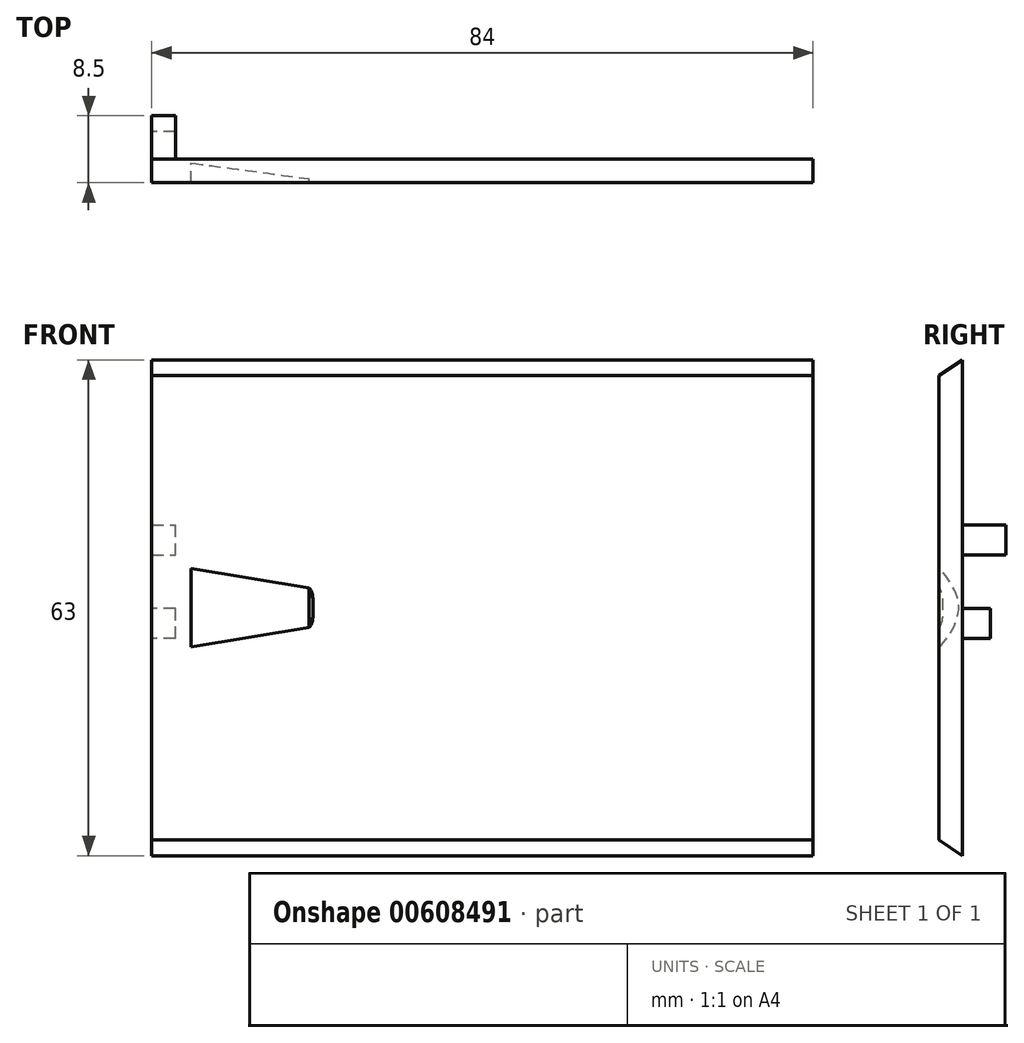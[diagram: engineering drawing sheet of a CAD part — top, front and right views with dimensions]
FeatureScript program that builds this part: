
annotation { "Feature Type Name" : "Feature", "Feature Type Description" : "" }
export const myFeature = defineFeature(function(context is Context, id is Id, definition is map)
    precondition{}
    {
        {
            var Q0;
            Q0=qCreatedBy(makeId("Front.planeOp"),FACE);
            var sketch = newSketch(context, id + "F0", { "sketchPlane" : qUnion([Q0])});
            skLineSegment(sketch, "E0.bottom", {"start": v(0, 0) * mm, "end": v(87, 0) * mm});
            skLineSegment(sketch, "E0.left", {"start": v(0, 0) * mm, "end": v(0, 81) * mm});
            skLineSegment(sketch, "E0.right", {"start": v(87, 0) * mm, "end": v(87, 81) * mm});
            skLineSegment(sketch, "E1", {"start": v(3, 3) * mm, "end": v(3, 35.5) * mm});
            skLineSegment(sketch, "E2", {"start": v(3, 35.5) * mm, "end": v(23.2, 35.5) * mm});
            skLineSegment(sketch, "E3", {"start": v(23.2, 35.5) * mm, "end": v(23.2, 37.5) * mm});
            skLineSegment(sketch, "E4", {"start": v(23.2, 37.5) * mm, "end": v(3, 37.5) * mm});
            skLineSegment(sketch, "E5", {"start": v(3, 37.5) * mm, "end": v(3, 43.2) * mm});
            skLineSegment(sketch, "E6", {"start": v(16.4, 45.2) * mm, "end": v(16.4, 42.3) * mm});
            skLineSegment(sketch, "E7", {"start": v(27.8, 41.8) * mm, "end": v(37.8, 41.8) * mm});
            skLineSegment(sketch, "E8", {"start": v(28.7, 37.5) * mm, "end": v(27.9, 37.5) * mm});
            skLineSegment(sketch, "E9", {"start": v(27.9, 37.5) * mm, "end": v(27.9, 35.5) * mm});
            skLineSegment(sketch, "E10", {"start": v(84, 62) * mm, "end": v(84, 3) * mm});
            skLineSegment(sketch, "E11", {"start": v(84, 3) * mm, "end": v(3, 3) * mm});
            skLineSegment(sketch, "E12", {"start": v(3.2, 37.6) * mm, "end": v(3.2, 39.1) * mm, "construction": true});
            skLineSegment(sketch, "E13", {"start": v(3.2, 39.1) * mm, "end": v(2.2, 39.1) * mm, "construction": true});
            skLineSegment(sketch, "E14", {"start": v(2.2, 39.1) * mm, "end": v(2.2, 43) * mm, "construction": true});
            skLineSegment(sketch, "E15", {"start": v(2.2, 43) * mm, "end": v(11.2, 43) * mm, "construction": true});
            skLineSegment(sketch, "E16", {"start": v(11.2, 43) * mm, "end": v(11.2, 42.1) * mm, "construction": true});
            skLineSegment(sketch, "E17", {"start": v(11.2, 42.1) * mm, "end": v(23.7, 42.1) * mm, "construction": true});
            skLineSegment(sketch, "E18", {"start": v(23.7, 42.1) * mm, "end": v(23.7, 42.6) * mm, "construction": true});
            skLineSegment(sketch, "E19", {"start": v(23.7, 42.6) * mm, "end": v(27.7, 42.6) * mm, "construction": true});
            skLineSegment(sketch, "E20", {"start": v(27.7, 35.6) * mm, "end": v(23.7, 35.6) * mm, "construction": true});
            skLineSegment(sketch, "E21", {"start": v(23.7, 35.6) * mm, "end": v(23.7, 37.6) * mm, "construction": true});
            skLineSegment(sketch, "E22", {"start": v(23.7, 37.6) * mm, "end": v(3.2, 37.6) * mm, "construction": true});
            skLineSegment(sketch, "E23", {"start": v(27.7, 35.6) * mm, "end": v(27.7, 37.6) * mm, "construction": true});
            skLineSegment(sketch, "E24", {"start": v(27.7, 37.6) * mm, "end": v(28.2, 37.6) * mm, "construction": true});
            skLineSegment(sketch, "E25", {"start": v(3, 43.2) * mm, "end": v(11.4, 43.2) * mm});
            skLineSegment(sketch, "E26", {"start": v(11.4, 43.2) * mm, "end": v(11.4, 42.3) * mm});
            skLineSegment(sketch, "E27", {"start": v(11.4, 42.3) * mm, "end": v(16.4, 42.3) * mm});
            skLineSegment(sketch, "E28", {"start": v(28.2, 37.6) * mm, "end": v(28.2, 39.6) * mm, "construction": true});
            skLineSegment(sketch, "E29", {"start": v(28.2, 39.6) * mm, "end": v(27.7, 39.6) * mm, "construction": true});
            skLineSegment(sketch, "E30", {"start": v(27.7, 39.6) * mm, "end": v(27.7, 42.6) * mm, "construction": true});
            skLineSegment(sketch, "E31.bottom", {"start": v(5, 3.5) * mm, "end": v(82, 3.5) * mm, "construction": true});
            skLineSegment(sketch, "E31.top", {"start": v(5, 25.5) * mm, "end": v(82, 25.5) * mm, "construction": true});
            skLineSegment(sketch, "E31.left", {"start": v(5, 3.5) * mm, "end": v(5, 25.5) * mm, "construction": true});
            skLineSegment(sketch, "E31.right", {"start": v(82, 3.5) * mm, "end": v(82, 25.5) * mm, "construction": true});
            skLineSegment(sketch, "E32", {"start": v(28.7, 37.5) * mm, "end": v(28.7, 39.8) * mm});
            skLineSegment(sketch, "E33", {"start": v(28.7, 39.8) * mm, "end": v(27.8, 39.8) * mm});
            skLineSegment(sketch, "E34", {"start": v(27.8, 39.8) * mm, "end": v(27.8, 41.8) * mm});
            skLineSegment(sketch, "E35", {"start": v(21.6, 54) * mm, "end": v(23.1, 54) * mm, "construction": true});
            skLineSegment(sketch, "E36", {"start": v(23.1, 54) * mm, "end": v(23.1, 52) * mm, "construction": true});
            skLineSegment(sketch, "E37", {"start": v(23.1, 52) * mm, "end": v(27.6, 52) * mm, "construction": true});
            skLineSegment(sketch, "E38", {"start": v(27.6, 52) * mm, "end": v(27.6, 54) * mm, "construction": true});
            skLineSegment(sketch, "E39", {"start": v(27.6, 54) * mm, "end": v(53.1, 54) * mm, "construction": true});
            skLineSegment(sketch, "E40", {"start": v(53.1, 54) * mm, "end": v(53.1, 52) * mm, "construction": true});
            skLineSegment(sketch, "E41", {"start": v(53.1, 52) * mm, "end": v(57.6, 52) * mm, "construction": true});
            skLineSegment(sketch, "E42", {"start": v(57.6, 52) * mm, "end": v(57.6, 54) * mm, "construction": true});
            skLineSegment(sketch, "E43", {"start": v(57.6, 54) * mm, "end": v(59.1, 54) * mm, "construction": true});
            skLineSegment(sketch, "E44", {"start": v(59.1, 54) * mm, "end": v(59.1, 55.5) * mm, "construction": true});
            skLineSegment(sketch, "E45", {"start": v(59.1, 55.5) * mm, "end": v(57.6, 55.5) * mm, "construction": true});
            skLineSegment(sketch, "E46", {"start": v(57.6, 55.5) * mm, "end": v(57.6, 61) * mm, "construction": true});
            skLineSegment(sketch, "E47", {"start": v(57.6, 61) * mm, "end": v(23.1, 61) * mm, "construction": true});
            skLineSegment(sketch, "E48", {"start": v(23.1, 61) * mm, "end": v(23.1, 55.5) * mm, "construction": true});
            skLineSegment(sketch, "E49", {"start": v(23.1, 55.5) * mm, "end": v(21.6, 55.5) * mm, "construction": true});
            skLineSegment(sketch, "E50", {"start": v(21.6, 55.5) * mm, "end": v(21.6, 54) * mm, "construction": true});
            skLineSegment(sketch, "E51", {"start": v(72.8, 60) * mm, "end": v(72.8, 57) * mm, "construction": true});
            skLineSegment(sketch, "E52", {"start": v(72.8, 57) * mm, "end": v(68.8, 57) * mm, "construction": true});
            skLineSegment(sketch, "E53", {"start": v(68.8, 57) * mm, "end": v(68.8, 47) * mm, "construction": true});
            skLineSegment(sketch, "E54", {"start": v(68.8, 47) * mm, "end": v(72.8, 47) * mm, "construction": true});
            skLineSegment(sketch, "E55", {"start": v(72.8, 47) * mm, "end": v(72.8, 43.5) * mm, "construction": true});
            skLineSegment(sketch, "E56", {"start": v(72.8, 43.5) * mm, "end": v(81.8, 43.5) * mm, "construction": true});
            skLineSegment(sketch, "E57", {"start": v(81.8, 43.5) * mm, "end": v(81.8, 35.5) * mm, "construction": true});
            skLineSegment(sketch, "E58", {"start": v(81.8, 35.5) * mm, "end": v(83.8, 35.5) * mm, "construction": true});
            skLineSegment(sketch, "E59", {"start": v(83.8, 35.5) * mm, "end": v(83.8, 47.5) * mm, "construction": true});
            skLineSegment(sketch, "E60", {"start": v(105.8, 47.5) * mm, "end": v(105.8, 54.5) * mm, "construction": true});
            skLineSegment(sketch, "E61", {"start": v(105.8, 54.5) * mm, "end": v(83.8, 54.5) * mm, "construction": true});
            skLineSegment(sketch, "E62", {"start": v(83.8, 54.5) * mm, "end": v(83.8, 60) * mm, "construction": true});
            skLineSegment(sketch, "E63", {"start": v(83.8, 60) * mm, "end": v(72.8, 60) * mm, "construction": true});
            skLineSegment(sketch, "E64", {"start": v(83.8, 47.5) * mm, "end": v(105.8, 47.5) * mm, "construction": true});
            skLineSegment(sketch, "E65", {"start": v(16.4, 45.2) * mm, "end": v(3, 45.2) * mm});
            skLineSegment(sketch, "E66", {"start": v(61.8, 62) * mm, "end": v(84, 62) * mm});
            skLineSegment(sketch, "E67", {"start": v(3, 45.2) * mm, "end": v(3, 62) * mm});
            skLineSegment(sketch, "E68", {"start": v(37.8, 41.8) * mm, "end": v(37.8, 35.5) * mm});
            skCircle(sketch, "E69", {"center": v(51.6, 58) * mm, "radius": 1.25 * mm, "construction": true});
            skLineSegment(sketch, "E70", {"start": v(57.8, 55.7) * mm, "end": v(59.3, 55.7) * mm});
            skLineSegment(sketch, "E71", {"start": v(59.3, 55.7) * mm, "end": v(59.3, 53.8) * mm});
            skLineSegment(sketch, "E72", {"start": v(59.3, 53.8) * mm, "end": v(57.8, 53.8) * mm});
            skLineSegment(sketch, "E73", {"start": v(57.8, 53.8) * mm, "end": v(57.8, 51.8) * mm});
            skLineSegment(sketch, "E74", {"start": v(57.8, 51.8) * mm, "end": v(61.8, 51.8) * mm});
            skLineSegment(sketch, "E75", {"start": v(61.8, 51.8) * mm, "end": v(61.8, 62) * mm});
            skLineSegment(sketch, "E76", {"start": v(57.8, 55.7) * mm, "end": v(57.8, 62) * mm});
            skLineSegment(sketch, "E77", {"start": v(57.8, 62) * mm, "end": v(22.9, 62) * mm});
            skLineSegment(sketch, "E78", {"start": v(22.9, 62) * mm, "end": v(22.9, 55.7) * mm});
            skLineSegment(sketch, "E79", {"start": v(22.9, 55.7) * mm, "end": v(21.4, 55.7) * mm});
            skLineSegment(sketch, "E80", {"start": v(21.4, 55.7) * mm, "end": v(21.4, 53.8) * mm});
            skLineSegment(sketch, "E81", {"start": v(21.4, 53.8) * mm, "end": v(22.9, 53.8) * mm});
            skLineSegment(sketch, "E82", {"start": v(22.9, 53.8) * mm, "end": v(22.9, 51.8) * mm});
            skLineSegment(sketch, "E83", {"start": v(22.9, 51.8) * mm, "end": v(18.9, 51.8) * mm});
            skLineSegment(sketch, "E84", {"start": v(18.9, 51.8) * mm, "end": v(18.9, 62) * mm});
            skLineSegment(sketch, "E85", {"start": v(18.9, 62) * mm, "end": v(3, 62) * mm});
            skLineSegment(sketch, "E86", {"start": v(37.8, 35.5) * mm, "end": v(27.9, 35.5) * mm});
            skLineSegment(sketch, "E87.bottom", {"start": v(34.85, 51.8) * mm, "end": v(45.85, 51.8) * mm});
            skLineSegment(sketch, "E87.top", {"start": v(34.85, 53.8) * mm, "end": v(45.85, 53.8) * mm});
            skLineSegment(sketch, "E87.left", {"start": v(34.85, 51.8) * mm, "end": v(34.85, 53.8) * mm});
            skLineSegment(sketch, "E87.right", {"start": v(45.85, 51.8) * mm, "end": v(45.85, 53.8) * mm});
            skLineSegment(sketch, "E88", {"start": v(27.6, 52) * mm, "end": v(34.85, 52) * mm, "construction": true});
            skLineSegment(sketch, "E89", {"start": v(53.1, 52) * mm, "end": v(45.85, 52) * mm, "construction": true});
            skLineSegment(sketch, "E90.bottom", {"start": v(14, 145.43) * mm, "end": v(74, 145.43) * mm, "construction": true});
            skLineSegment(sketch, "E90.top", {"start": v(14, 85.43) * mm, "end": v(74, 85.43) * mm, "construction": true});
            skLineSegment(sketch, "E90.left", {"start": v(14, 145.43) * mm, "end": v(14, 85.43) * mm, "construction": true});
            skLineSegment(sketch, "E90.right", {"start": v(74, 145.43) * mm, "end": v(74, 85.43) * mm, "construction": true});
            skPoint(sketch, "E91", {"position": v(44, 65) * mm});
            skLineSegment(sketch, "E92", {"start": v(44, 65) * mm, "end": v(44, 115.43) * mm, "construction": true});
            skCircle(sketch, "E93", {"center": v(44, 115.43) * mm, "radius": 30 * mm});
            skCircle(sketch, "E94", {"center": v(44, 115.43) * mm, "radius": 42.43 * mm});
            skLineSegment(sketch, "E95.bottom", {"start": v(1, 77) * mm, "end": v(87, 77) * mm});
            skLineSegment(sketch, "E95.top", {"start": v(1, 69) * mm, "end": v(87, 69) * mm});
            skLineSegment(sketch, "E95.left", {"start": v(1, 77) * mm, "end": v(1, 69) * mm});
            skLineSegment(sketch, "E95.right", {"start": v(87, 77) * mm, "end": v(87, 69) * mm});
            skPoint(sketch, "E95.middle", {"position": v(44, 73) * mm});
            skLineSegment(sketch, "E96", {"start": v(0, 81) * mm, "end": v(8, 81) * mm});
            skLineSegment(sketch, "E97", {"start": v(8, 81) * mm, "end": v(8, 65) * mm});
            skLineSegment(sketch, "E98", {"start": v(8, 65) * mm, "end": v(79, 65) * mm});
            skLineSegment(sketch, "E99", {"start": v(79, 65) * mm, "end": v(79, 81) * mm});
            skLineSegment(sketch, "E100", {"start": v(79, 81) * mm, "end": v(87, 81) * mm});
            skLineSegment(sketch, "E101.bottom", {"start": v(3, 37.5) * mm, "end": v(28.7, 37.5) * mm});
            skLineSegment(sketch, "E101.top", {"start": v(3, 39) * mm, "end": v(28.7, 39) * mm});
            skLineSegment(sketch, "E101.left", {"start": v(3, 37.5) * mm, "end": v(3, 39) * mm});
            skLineSegment(sketch, "E101.right", {"start": v(28.7, 37.5) * mm, "end": v(28.7, 39) * mm});
            skLineSegment(sketch, "E102.bottom", {"start": v(21.4, 53.8) * mm, "end": v(59.3, 53.8) * mm});
            skLineSegment(sketch, "E102.top", {"start": v(21.4, 55.7) * mm, "end": v(59.3, 55.7) * mm});
            skLineSegment(sketch, "E102.left", {"start": v(21.4, 53.8) * mm, "end": v(21.4, 55.7) * mm});
            skLineSegment(sketch, "E102.right", {"start": v(59.3, 53.8) * mm, "end": v(59.3, 55.7) * mm});
            skPoint(sketch, "E103", {"position": v(105.8, 51) * mm});
            skLineSegment(sketch, "E104", {"start": v(105.8, 51) * mm, "end": v(68.8, 51) * mm, "construction": true});
            skLineSegment(sketch, "E105", {"start": v(5, 25.5) * mm, "end": v(5, 35.5) * mm, "construction": true});
            skPoint(sketch, "E106", {"position": v(5, 30.5) * mm});
            skLineSegment(sketch, "E107", {"start": v(3, 30.5) * mm, "end": v(0, 30.5) * mm, "construction": true});
            skPoint(sketch, "E108", {"position": v(1.5, 30.5) * mm});
            skLineSegment(sketch, "E109.bottom", {"start": v(3, 32.4) * mm, "end": v(0, 32.4) * mm});
            skLineSegment(sketch, "E109.top", {"start": v(3, 28.6) * mm, "end": v(0, 28.6) * mm});
            skLineSegment(sketch, "E109.left", {"start": v(3, 32.4) * mm, "end": v(3, 28.6) * mm});
            skLineSegment(sketch, "E109.right", {"start": v(0, 32.4) * mm, "end": v(0, 28.6) * mm});
            skSolve(sketch);
        }
        {
            var Q0;
            Q0=qCreatedBy(makeId("Front.planeOp"),FACE);
            var sketch = newSketch(context, id + "F1", { "sketchPlane" : qUnion([Q0])});
            skLineSegment(sketch, "E110.bottom", {"start": v(0, 65) * mm, "end": v(84, 65) * mm});
            skLineSegment(sketch, "E110.top", {"start": v(0, 0) * mm, "end": v(84, 0) * mm});
            skLineSegment(sketch, "E110.left", {"start": v(0, 65) * mm, "end": v(0, 0) * mm});
            skLineSegment(sketch, "E110.right", {"start": v(84, 65) * mm, "end": v(84, 0) * mm});
            skSolve(sketch);
        }
        {
            var Q0;
            Q0 = qSketchRegion(id + "F1", true);
            extrude(context, id + "F2", {"entities" : qUnion([Q0]), "depth" : 3 * mm, "offsetDistance" : 25 * mm});
        }
        {
            var Q0;
            {var subQ5=sQuery(id+"F0.wireOp",EDGE,"E0.bottom");Q0=makeQuery(id+"F0.imprint","IMPRINT",FACE,{"disambiguationData":[TD([[makeQuery(id+"F0.imprint","IMPRINT",EDGE,{"derivedFrom":subQ5}),1.0]])]});}
            var sketch = newSketch(context, id + "F3", { "sketchPlane" : qUnion([Q0])});
            skLineSegment(sketch, "E111.bottom", {"start": v(0, 43) * mm, "end": v(3, 43) * mm});
            skLineSegment(sketch, "E111.top", {"start": v(0, 39.2) * mm, "end": v(3, 39.2) * mm});
            skLineSegment(sketch, "E111.left", {"start": v(0, 43) * mm, "end": v(0, 39.2) * mm});
            skLineSegment(sketch, "E111.right", {"start": v(3, 43) * mm, "end": v(3, 39.2) * mm});
            skSolve(sketch);
        }
        {
            var Q0;
            Q0 = qSketchRegion(id + "F3", true);
            extrude(context, id + "F4", {"entities" : qUnion([Q0]), "operationType" : NewBodyOperationType.ADD, "oppositeDirection" : true, "depth" : 5.5 * mm, "offsetDistance" : 25 * mm});
        }
        {
            var Q0;
            Q0=makeQuery(id+"F4.boolean.opBoolean","MERGE",FACE,{"derivedFrom":[makeQuery(id+"F2.opExtrude","SWEPT_FACE",FACE,{"disambiguationData":[OSD([sQuery(id+"F1.wireOp",EDGE,"E110.left")])]}),makeQuery(id+"F4.opExtrude","SWEPT_FACE",FACE,{"disambiguationData":[OSD([sQuery(id+"F3.wireOp",EDGE,"E111.left")])]})]});
            var sketch = newSketch(context, id + "F5", { "sketchPlane" : qUnion([Q0])});
            skLineSegment(sketch, "E112", {"start": v(0, 65) * mm, "end": v(3, 65) * mm});
            skLineSegment(sketch, "E113", {"start": v(3, 65) * mm, "end": v(3, 62) * mm});
            skLineSegment(sketch, "E114", {"start": v(3, 62) * mm, "end": v(0, 64) * mm});
            skLineSegment(sketch, "E115", {"start": v(0, 64) * mm, "end": v(0, 65) * mm});
            skLineSegment(sketch, "E116", {"start": v(0, 0) * mm, "end": v(3, 0) * mm});
            skLineSegment(sketch, "E117", {"start": v(3, 0) * mm, "end": v(3, 3) * mm});
            skLineSegment(sketch, "E118", {"start": v(3, 3) * mm, "end": v(0, 1) * mm});
            skLineSegment(sketch, "E119", {"start": v(0, 1) * mm, "end": v(0, 0) * mm});
            skSolve(sketch);
        }
        {
            var Q0;
            Q0 = qSketchRegion(id + "F5", true);
            var Q1;
            Q1=sQuery(id+"F0.wireOp",EDGE,"E0.bottom");
            sweep(context, id + "F6", {"operationType" : NewBodyOperationType.REMOVE, "profiles" : qUnion([Q0]), "path" : qUnion([Q1])});
        }
        {
            var Q0;
            Q0=makeQuery(id+"F2.opExtrude","CAP_FACE",FACE,{"disambiguationData":[OSD([sQuery(id+"F1.wireOp",EDGE,"E110.bottom"),sQuery(id+"F1.wireOp",EDGE,"E110.top"),sQuery(id+"F1.wireOp",EDGE,"E110.left"),sQuery(id+"F1.wireOp",EDGE,"E110.right")])],"isStart":false});
            var sketch = newSketch(context, id + "F7", { "sketchPlane" : qUnion([Q0])});
            skLineSegment(sketch, "E120", {"start": v(5, 40) * mm, "end": v(5, 0) * mm, "construction": true});
            skLineSegment(sketch, "E121", {"start": v(20, 40) * mm, "end": v(20, 0) * mm, "construction": true});
            skSolve(sketch);
        }
        {
            var Q0;
            Q0=sQuery(id+"F7.wireOp",EDGE,"E120");
            cPlane(context, id + "F8", {"entities" : qUnion([Q0]), "cplaneType" : CPlaneType.LINE_ANGLE, "offset" : 25 * mm, "angle" : 0 * degree, "width" : 150 * mm, "height" : 150 * mm});
        }
        {
            var Q0;
            Q0=qCreatedBy(id+"F8.planeOp",FACE);
            var sketch = newSketch(context, id + "F9", { "sketchPlane" : qUnion([Q0])});
            skLineSegment(sketch, "E122", {"start": v(3, 37.5) * mm, "end": v(3, 27.5) * mm});
            skFitSpline(sketch, "E123", {"points": [v(3, 27.5) * mm, v(0.5, 32.5) * mm, v(3, 37.5) * mm], "startDerivative": vector(-6, 6) * mm, "endDerivative": vector(6, 6) * mm});
            skLineSegment(sketch, "E124", {"start": v(0, 1) * mm, "end": v(0, 64) * mm, "construction": true});
            skPoint(sketch, "E125", {"position": v(0, 32.5) * mm});
            skLineSegment(sketch, "E126", {"start": v(0, 32.5) * mm, "end": v(3, 32.5) * mm, "construction": true});
            skSolve(sketch);
        }
        {
            var Q0;
            Q0=sQuery(id+"F7.wireOp",EDGE,"E121");
            cPlane(context, id + "F10", {"entities" : qUnion([Q0]), "cplaneType" : CPlaneType.LINE_ANGLE, "offset" : 25 * mm, "angle" : 0 * degree, "width" : 150 * mm, "height" : 150 * mm});
        }
        {
            var Q0;
            Q0=qCreatedBy(id+"F10.planeOp",FACE);
            var sketch = newSketch(context, id + "F11", { "sketchPlane" : qUnion([Q0])});
            skLineSegment(sketch, "E127", {"start": v(3, 35) * mm, "end": v(3, 30) * mm});
            skFitSpline(sketch, "E128", {"points": [v(3, 30) * mm, v(2.5, 32.5) * mm, v(3, 35) * mm], "startDerivative": vector(-3, 3) * mm, "endDerivative": vector(3, 3) * mm});
            skSolve(sketch);
        }
        {
            var Q0;
            Q0 = qSketchRegion(id + "F11", true);
            var Q1;
            Q1 = qSketchRegion(id + "F9", true);
            loft(context, id + "F12", {"operationType" : NewBodyOperationType.REMOVE, "sheetProfilesArray" : [{ "sheetProfileEntities" : qUnion([Q0]) }, { "sheetProfileEntities" : qUnion([Q1]) }]});
        }
        {
            var Q0;
            Q0 = qSketchRegion(id + "F11", true);
            var Q1;
            Q1=sQuery(id+"F7.wireOp",EDGE,"E121");
            revolve(context, id + "F13", {"operationType" : NewBodyOperationType.REMOVE, "entities" : qUnion([Q0]), "axis" : qUnion([Q1]), "revolveType" : RevolveType.FULL, "oppositeDirection" : true});
        }
        {
            var Q0;
            Q0=makeQuery(id+"F0.imprint","IMPRINT",FACE,{"disambiguationData":[TD([[makeQuery(id+"F0.imprint","IMPRINT",EDGE,{"derivedFrom":sQuery(id+"F0.wireOp",EDGE,"E109.bottom")}),1.0]])]});
            extrude(context, id + "F14", {"entities" : qUnion([Q0]), "operationType" : NewBodyOperationType.ADD, "oppositeDirection" : true, "depth" : 3.5 * mm, "offsetDistance" : 25 * mm});
        }
    });
